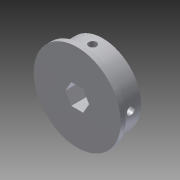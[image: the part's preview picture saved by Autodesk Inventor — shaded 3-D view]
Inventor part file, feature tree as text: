
AUTODESK INVENTOR PART (.ipt)
format: ipt  version: 2014 (Build 180170000, 170)  size: 158,720 bytes
history: native  units: in
note: dims shown in document units (in); Inventor stores cm internally (conversion verified against a paired STEP export)
features: extrude x6, sketch x6, plane x5, fillet x1, projected_geometry x1
ambient origin geometry x8: Origin, YZ Plane, XZ Plane, XY Plane, X Axis, Y Axis, Z Axis, Center Point
bodies: Solid1 (feature_tree)
feature tree (19):
  extrude  "Extrusion1"  Depth=0.502in
  plane  "Work Plane1"
  extrude  "Extrusion2"  Depth=0.5in
  plane  "Work Plane2"
  extrude  "Extrusion3"  Depth=0.2188in TaperAngle=0.0deg
  plane  "Work Plane4"
  extrude  "Extrusion4"  Depth=0.25in
  plane  "Work Plane5"
  extrude  "Extrusion5"  TaperAngle=150.0deg  [1 undecoded]
  extrude  "Extrusion6"  Depth=0.125in
  fillet  "Fillet1"  Radius=0.2188in
  sketch  "Sketch1"  dims[d0=1.873in d2=0.502in]
  sketch  "Sketch2"  dims[d3=0.5in d4=0.0in d5=0.19in]
  projected_geometry  "Projected Loop1"
  sketch  "Sketch3"  dims[d6=0.25in d7=0.2188in d8=0.0in]
  plane  "Work Plane3"
  sketch  "Sketch4"  dims[d9=0.19in d10=0.25in]
  sketch  "Sketch5"  dims[d11=0.2188in d12=0.0in d13=150.0deg]
  sketch  "Sketch6"  dims[d14=0.19in d15=0.25in d16=0.2188in d17=0.0in d18=0.19in d19=0.25in d20=0.2188in d21=0.0in d23=0.125in d24=0.0in d25=0.0312in d26=0.125in]
note: 1 required parameter value undecoded (feature->parameter linkage not recoverable at this tier; creation-order binding heuristic only, values carry confidence <= 0.55)
